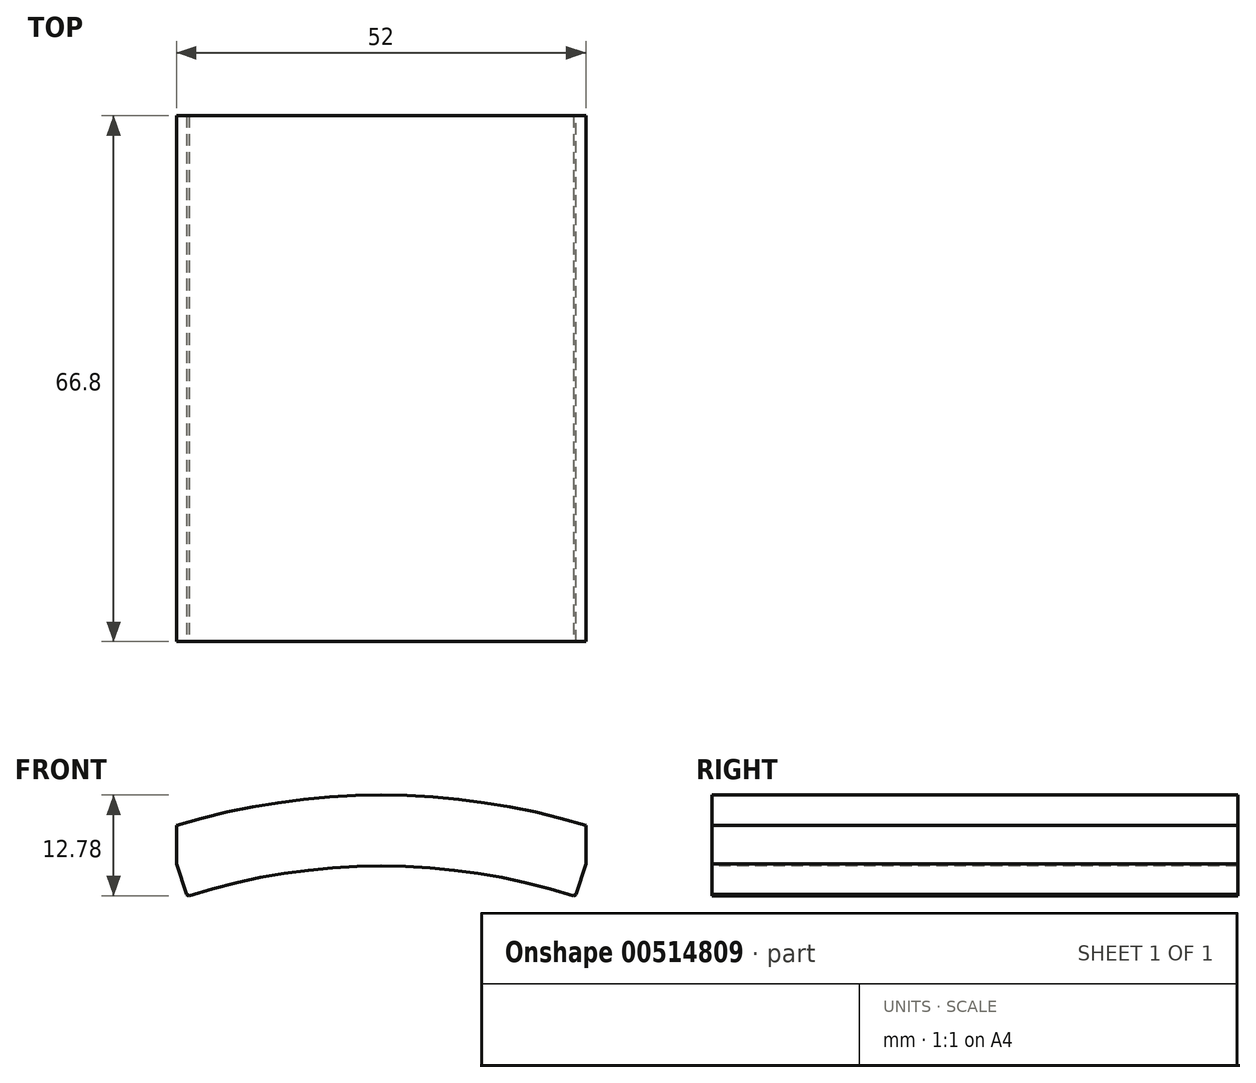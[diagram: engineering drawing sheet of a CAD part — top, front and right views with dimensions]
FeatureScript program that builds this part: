
annotation { "Feature Type Name" : "Feature", "Feature Type Description" : "" }
export const myFeature = defineFeature(function(context is Context, id is Id, definition is map)
    precondition{}
    {
        {
            var Q0;
            Q0=qCreatedBy(makeId("Front.planeOp"),FACE);
            var sketch = newSketch(context, id + "F0", { "sketchPlane" : qUnion([Q0])});
            skLineSegment(sketch, "E0", {"start": v(26, 80.02) * mm, "end": v(0, 0) * mm, "construction": true});
            skLineSegment(sketch, "E1", {"start": v(0, 0) * mm, "end": v(0, 89.75) * mm, "construction": true});
            skArc(sketch, "E2", {"start": v(-27.55, 85.42) * mm, "mid": v(26.78, -85.66) * mm, "end": v(-26, 85.9) * mm, "construction": true});
            skLineSegment(sketch, "E3.0", {"start": v(26, 81.04) * mm, "end": v(26, 85.9) * mm});
            skLineSegment(sketch, "E4", {"start": v(0, 0) * mm, "end": v(24.79, 76.85) * mm, "construction": true});
            skLineSegment(sketch, "E5.MirrorCS", {"start": v(-26, 81.04) * mm, "end": v(-26, 85.9) * mm});
            skArc(sketch, "E6.trimOffspring", {"start": v(26, 85.9) * mm, "mid": v(0, 89.75) * mm, "end": v(-26, 85.9) * mm});
            skLineSegment(sketch, "E7.MirrorCS", {"start": v(0, 0) * mm, "end": v(-24.79, 76.85) * mm, "construction": true});
            skLineSegment(sketch, "E8.0", {"start": v(25.71, 80.11) * mm, "end": v(-0.29, 0.1) * mm, "construction": true});
            skLineSegment(sketch, "E9", {"start": v(26, 81.04) * mm, "end": v(24.67, 76.89) * mm});
            skLineSegment(sketch, "E10.MirrorCS", {"start": v(-26, 81.04) * mm, "end": v(-24.67, 76.89) * mm});
            skLineSegment(sketch, "E11.trimOffspring", {"start": v(-0.16, 0.49) * mm, "end": v(0, 0) * mm});
            skPoint(sketch, "E12.start.orphan", {"position": v(26, 80.62) * mm});
            skArc(sketch, "E13", {"start": v(24.67, 76.89) * mm, "mid": v(0, 80.75) * mm, "end": v(-24.67, 76.89) * mm});
            skSolve(sketch);
        }
        {
            var Q0;
            Q0=makeQuery(id+"F0.imprint","IMPRINT",FACE,{"disambiguationData":[TD([[makeQuery(id+"F0.imprint","IMPRINT",EDGE,{"derivedFrom":sQuery(id+"F0.wireOp",EDGE,"E3.0")}),1.0]])]});
            extrude(context, id + "F1", {"entities" : qUnion([Q0]), "oppositeDirection" : true, "depth" : 66.8 * mm, "offsetDistance" : 25 * mm});
        }
        {
            var Q0;
            Q0=makeQuery(id+"F1.opExtrude","SWEPT_EDGE",EDGE,{"disambiguationData":[OSD([sQuery(id+"F0.wireOp",EDGE,"E9"),sQuery(id+"F0.wireOp",EDGE,"E13")])]});
            var Q1;
            Q1=makeQuery(id+"F1.opExtrude","SWEPT_EDGE",EDGE,{"disambiguationData":[OSD([sQuery(id+"F0.wireOp",EDGE,"E10.MirrorCS"),sQuery(id+"F0.wireOp",EDGE,"E13")])]});
            chamfer(context, id + "F2", {"entities" : qUnion([Q0, Q1]), "width" : .25 * mm, "tangentPropagation" : true});
        }
    });
